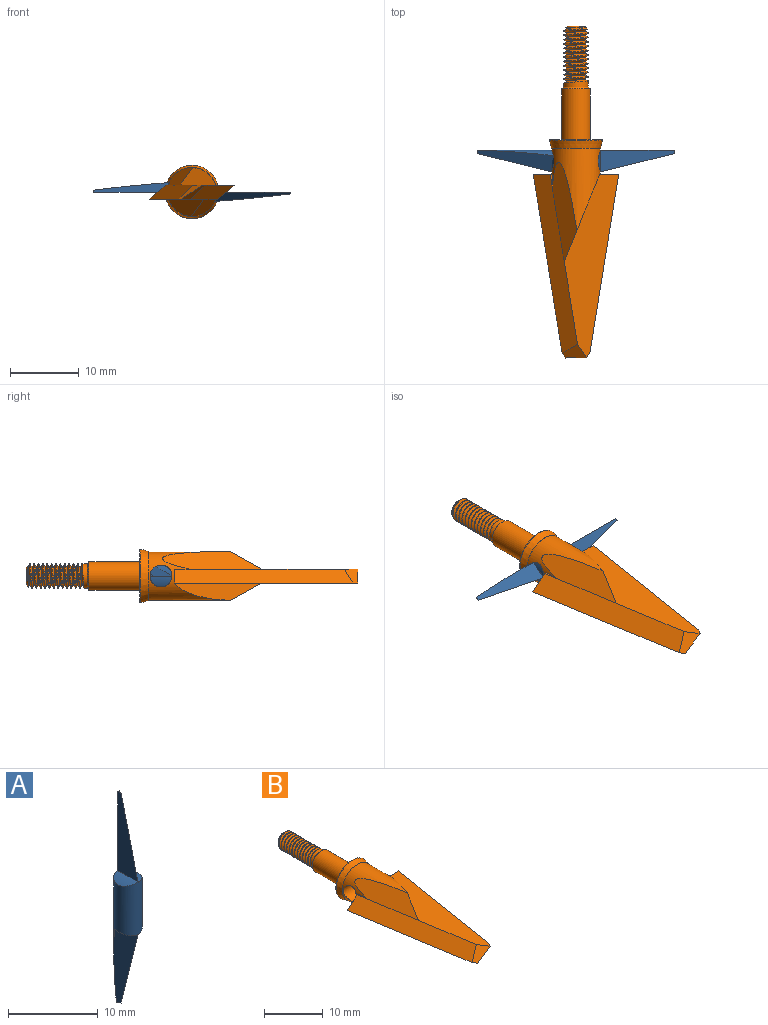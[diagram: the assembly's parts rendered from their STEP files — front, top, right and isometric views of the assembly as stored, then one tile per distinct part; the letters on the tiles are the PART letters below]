
ASSEMBLY  parts=2 mates=1
PART A: 13 faces, bbox 3.3x3.3x28.7 mm
  f0: cylinder r=1.59mm len=28.58mm, axis (0,0,-1), area 87.8mm2, adj f1,f2,f3,f4,f6,f7,f8,f9
  f1: cylinder r=3.56mm len=2.38mm, axis (0,1,0), area 1.6mm2, adj f0,f5,f9,f12
  f2: plane 10.73x3.18mm, normal (-1,0,0), area 19.8mm2, adj f0,f4,f7,f11
  f3: cylinder r=3.56mm len=3.18mm, axis (0,1,0), area 4.1mm2, adj f0,f6
  f4: plane 11.09x3.24mm, normal (0.87,-0.49,0.12), area 19.3mm2, adj f0,f2,f8,f11
  f5: plane 0.07x0.04mm, normal (-0.5,0.86,0.12), area 0mm2, adj f1,f9,f12
  f6: plane 10.73x3.18mm, normal (1,0,0), area 19.8mm2, adj f0,f3,f9,f10
  f7: cylinder r=3.56mm len=3.18mm, axis (0,1,0), area 4.1mm2, adj f0,f2
  f8: cylinder r=3.56mm len=2.38mm, axis (0,1,0), area 1.6mm2, adj f0,f4
  f9: plane 11.03x3.17mm, normal (-0.87,-0.49,-0.12), area 19.3mm2, adj f0,f1,f5,f6,f10,f12
  f10: plane 0.51x0.27mm, normal (0,0,-1), area 0.1mm2, adj f0,f6,f9
  f11: plane 0.51x0.27mm, normal (0,0,1), area 0.1mm2, adj f0,f2,f4
  f12: plane 1.08x0.59mm, normal (0.08,0.11,-0.99), area 0.1mm2, adj f1,f5,f9
PART B: 43 faces, bbox 12.4x48.4x8.4 mm
  f0: cylinder r=2.08mm len=7.37mm, axis (0,-1,0), area 96.4mm2, adj f2,f4
  f1: plane 3.66x3.66mm, normal (0,1,0), area 0.9mm2, adj f2,f24
  f2: cone r=1.83mm half-angle=45deg, axis (0,-1,0), area 4.4mm2, adj f0,f1
  f3: cone r=3.94mm half-angle=16deg, axis (0,1,0), area 27mm2, adj f5,f6
  f4: plane 7.54x7.54mm, normal (0,1,0), area 31mm2, adj f0,f6
  f5: plane 7.15x7.15mm, normal (0,-1,0), area 0.4mm2, adj f3,f22
  f6: torus R=3.77mm, axis (0,1,0), area 5.7mm2, adj f3,f4
  f7: plane 14.43x3.54mm, normal (-0.7,-0.11,0.71), area 38.8mm2, adj f17,f18,f22
  f8: plane 2.8x2.03mm, normal (0,1,0), area 3mm2, adj f10,f14,f16,f22
  f9: plane 26.67x7.91mm, normal (0,0,-1), area 104.3mm2, adj f12,f13,f15,f16,f17,f20,f21
  f10: plane 26.67x7.91mm, normal (0,0,1), area 104.3mm2, adj f8,f13,f15,f16,f17,f18
  f11: plane 2.13x0.34mm, normal (0,0,1), area 0.4mm2, adj f12,f17,f22
  f12: plane 2.8x2.03mm, normal (0,1,0), area 3mm2, adj f9,f11,f17,f22
  f13: plane 3.55x2.03mm, normal (-0.52,-0.34,0.78), area 5.3mm2, adj f9,f10,f15,f17
  f14: plane 2.13x0.34mm, normal (0,0,-1), area 0.4mm2, adj f8,f16,f22
  f15: plane 3.55x2.03mm, normal (0.52,-0.34,-0.78), area 5.3mm2, adj f9,f10,f13,f16
  f16: plane 25.9x6.43mm, normal (0.63,-0.1,-0.77), area 81mm2, adj f8,f9,f10,f14,f15,f19
  f17: plane 25.9x6.43mm, normal (-0.63,-0.1,0.77), area 81mm2, adj f7,f9,f10,f11,f12,f13
  f18: plane 12.69x5.11mm, normal (0.93,-0.37,0), area 22.4mm2, adj f7,f10,f22
  f19: plane 14.45x3.55mm, normal (0.7,-0.11,-0.71), area 38.9mm2, adj f16,f20,f21,f22
  f20: plane 0x0mm, normal (0,-1,0), area 0mm2, adj f9,f19,f21
  f21: plane 12.7x5.11mm, normal (-0.93,-0.37,0), area 22.4mm2, adj f9,f19,f20,f22
  f22: cylinder r=3.56mm len=11.95mm, axis (0,-1,0), area 107.3mm2, adj f5,f7,f8,f11,f12,f14,f18,f19
  f23: cylinder r=1.59mm len=6.82mm, axis (-1,0,0), area 68mm2, adj f22
  f24: cylinder r=1.75mm len=3.51mm, axis (0,-1,0), area 7.4mm2, adj f1,f25,f39,f41,f42
  f25: cylinder r=1.75mm len=3.51mm, axis (0,-1,0), area 1mm2, adj f24,f26,f41,f42
  f26: cylinder r=1.75mm len=3.51mm, axis (0,-1,0), area 1mm2, adj f25,f27,f41,f42
  f27: cylinder r=1.75mm len=3.51mm, axis (0,-1,0), area 1mm2, adj f26,f28,f41,f42
  f28: cylinder r=1.75mm len=3.51mm, axis (0,-1,0), area 1mm2, adj f27,f29,f41,f42
  f29: cylinder r=1.75mm len=3.51mm, axis (0,-1,0), area 1mm2, adj f28,f30,f41,f42
  f30: cylinder r=1.75mm len=3.51mm, axis (0,-1,0), area 1mm2, adj f29,f31,f41,f42
  f31: cylinder r=1.75mm len=3.51mm, axis (0,-1,0), area 1mm2, adj f30,f32,f41,f42
  f32: cylinder r=1.75mm len=3.51mm, axis (0,-1,0), area 1mm2, adj f31,f33,f41,f42
  f33: cylinder r=1.75mm len=3.51mm, axis (0,-1,0), area 1mm2, adj f32,f34,f41,f42
  f34: cylinder r=1.75mm len=3.51mm, axis (0,-1,0), area 1mm2, adj f33,f35,f41,f42
  f35: cylinder r=1.75mm len=3.51mm, axis (0,-1,0), area 1mm2, adj f34,f36,f41,f42
  f36: cylinder r=1.75mm len=1.33mm, axis (0,-1,0), area 0.1mm2, adj f35,f38,f41
  f37: plane 2.49x2.49mm, normal (0,1,0), area 4.9mm2, adj f38
  f38: cone r=1.24mm half-angle=45deg, axis (0,-1,0), area 4mm2, adj f36,f37,f40,f41,f42
  f39: plane 0.55x0.37mm, normal (0,0,-1), area 0.1mm2, adj f24,f40,f41,f42
  f40: cylinder r=1.38mm len=8.25mm, axis (0,1,0), area 13.7mm2, adj f38,f39,f41,f42
  f41: bspline ~8.36x4.05mm, area 51.9mm2, adj f24,f25,f26,f27,f28,f29,f30,f31
  f42: bspline ~8.47x4.05mm, area 54.2mm2, adj f24,f25,f26,f27,f28,f29,f30,f31
PLACE A rot(axis=(0,1,0),90deg) t=(0,1.96,0)mm
PLACE B at identity fixed
MATE cylindrical B.f23 <-> A.f0  axis (-1,0,0) through (0,1.96,0)mm
